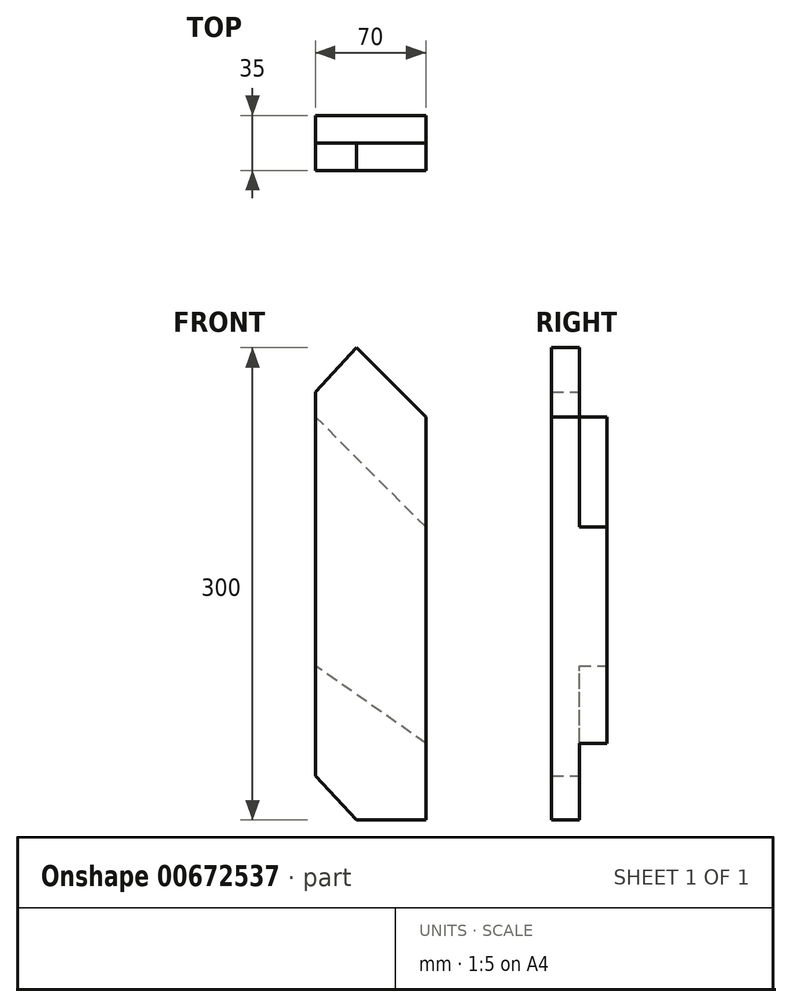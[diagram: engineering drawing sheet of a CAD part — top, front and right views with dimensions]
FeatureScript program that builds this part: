
annotation { "Feature Type Name" : "Feature", "Feature Type Description" : "" }
export const myFeature = defineFeature(function(context is Context, id is Id, definition is map)
    precondition{}
    {
        {
            var Q0;
            Q0=qCreatedBy(makeId("Front.planeOp"),FACE);
            var sketch = newSketch(context, id + "F0", { "sketchPlane" : qUnion([Q0])});
            skLineSegment(sketch, "E0.bottom", {"start": v(0, 0) * mm, "end": v(70, 0) * mm});
            skLineSegment(sketch, "E0.top", {"start": v(0, 300) * mm, "end": v(70, 300) * mm});
            skLineSegment(sketch, "E0.left", {"start": v(0, 0) * mm, "end": v(0, 300) * mm});
            skLineSegment(sketch, "E0.right", {"start": v(70, 0) * mm, "end": v(70, 300) * mm});
            skSolve(sketch);
        }
        {
            var Q0;
            Q0=makeQuery(id+"F0.imprint","IMPRINT",FACE,{"disambiguationData":[TD([[makeQuery(id+"F0.imprint","IMPRINT",EDGE,{"derivedFrom":sQuery(id+"F0.wireOp",EDGE,"E0.bottom")}),1.0]])]});
            extrude(context, id + "F1", {"entities" : qUnion([Q0]), "depth" : 35 * mm, "offsetDistance" : 25 * mm});
        }
        {
            var Q0;
            Q0=makeQuery(id+"F1.opExtrude","CAP_FACE",FACE,{"disambiguationData":[OSD([sQuery(id+"F0.wireOp",EDGE,"E0.bottom"),sQuery(id+"F0.wireOp",EDGE,"E0.top"),sQuery(id+"F0.wireOp",EDGE,"E0.left"),sQuery(id+"F0.wireOp",EDGE,"E0.right")])],"isStart":true});
            var sketch = newSketch(context, id + "F2", { "sketchPlane" : qUnion([Q0])});
            skLineSegment(sketch, "E1", {"start": v(-70, 300) * mm, "end": v(-70, 256) * mm});
            skLineSegment(sketch, "E2", {"start": v(-70, 300) * mm, "end": v(-26, 300) * mm});
            skLineSegment(sketch, "E3", {"start": v(0, 300) * mm, "end": v(0, 272) * mm});
            skLineSegment(sketch, "E4", {"start": v(-26, 300) * mm, "end": v(0, 300) * mm});
            skLineSegment(sketch, "E5", {"start": v(-26, 300) * mm, "end": v(-70, 256) * mm});
            skLineSegment(sketch, "E6", {"start": v(-26, 300) * mm, "end": v(0, 272) * mm});
            skSolve(sketch);
        }
        {
            var Q0;
            Q0=makeQuery(id+"F2.imprint","IMPRINT",FACE,{"disambiguationData":[TD([[makeQuery(id+"F2.imprint","IMPRINT",EDGE,{"derivedFrom":sQuery(id+"F2.wireOp",EDGE,"E1")}),-1.0]])]});
            var Q1;
            Q1=makeQuery(id+"F2.imprint","IMPRINT",FACE,{"disambiguationData":[TD([[makeQuery(id+"F2.imprint","IMPRINT",EDGE,{"derivedFrom":sQuery(id+"F2.wireOp",EDGE,"E3")}),1.0]])]});
            extrude(context, id + "F3", {"entities" : qUnion([Q0, Q1]), "operationType" : NewBodyOperationType.REMOVE, "endBound" : BoundingType.THROUGH_ALL, "oppositeDirection" : true, "depth" : 25 * mm, "offsetDistance" : 25 * mm});
        }
        {
            var Q0;
            Q0=makeQuery(id+"F1.opExtrude","SWEPT_FACE",FACE,{"disambiguationData":[OSD([sQuery(id+"F0.wireOp",EDGE,"E0.left")])]});
            var sketch = newSketch(context, id + "F4", { "sketchPlane" : qUnion([Q0])});
            skLineSegment(sketch, "E7", {"start": v(0, 69.18) * mm, "end": v(0, 69.18) * mm});
            skSolve(sketch);
        }
        {
            var Q0;
            Q0=makeQuery(id+"F1.opExtrude","CAP_FACE",FACE,{"disambiguationData":[OSD([sQuery(id+"F0.wireOp",EDGE,"E0.bottom"),sQuery(id+"F0.wireOp",EDGE,"E0.top"),sQuery(id+"F0.wireOp",EDGE,"E0.left"),sQuery(id+"F0.wireOp",EDGE,"E0.right")])],"isStart":true});
            var sketch = newSketch(context, id + "F5", { "sketchPlane" : qUnion([Q0])});
            skLineSegment(sketch, "E8", {"start": v(-70, 186) * mm, "end": v(0, 256) * mm});
            skSolve(sketch);
        }
        {
            var Q0;
            {var subQ3=sQuery(id+"F5.wireOp",EDGE,"E8");Q0=makeQuery(id+"F5.imprint","IMPRINT",FACE,{"disambiguationData":[TD([[makeQuery(id+"F5.imprint","IMPRINT",EDGE,{"derivedFrom":subQ3}),1.0]])]});}
            extrude(context, id + "F6", {"entities" : qUnion([Q0]), "operationType" : NewBodyOperationType.REMOVE, "oppositeDirection" : true, "depth" : 17.5 * mm, "offsetDistance" : 25 * mm});
        }
        {
            var Q0;
            Q0=makeQuery(id+"F1.opExtrude","CAP_FACE",FACE,{"disambiguationData":[OSD([sQuery(id+"F0.wireOp",EDGE,"E0.bottom"),sQuery(id+"F0.wireOp",EDGE,"E0.top"),sQuery(id+"F0.wireOp",EDGE,"E0.left"),sQuery(id+"F0.wireOp",EDGE,"E0.right")])],"isStart":true});
            var sketch = newSketch(context, id + "F7", { "sketchPlane" : qUnion([Q0])});
            skLineSegment(sketch, "E9", {"start": v(-70, 48.73) * mm, "end": v(0, 98) * mm});
            skLineSegment(sketch, "E10", {"start": v(-70, 0) * mm, "end": v(-26, 0) * mm});
            skLineSegment(sketch, "E11", {"start": v(-26, 0) * mm, "end": v(0, 0) * mm});
            skLineSegment(sketch, "E12", {"start": v(0, 0) * mm, "end": v(0, 28) * mm});
            skLineSegment(sketch, "E13", {"start": v(0, 28) * mm, "end": v(-26, 0) * mm});
            skSolve(sketch);
        }
        {
            var Q0;
            Q0=makeQuery(id+"F7.imprint","IMPRINT",FACE,{"disambiguationData":[TD([[makeQuery(id+"F7.imprint","IMPRINT",EDGE,{"derivedFrom":sQuery(id+"F7.wireOp",EDGE,"E11")}),-1.0]])]});
            extrude(context, id + "F8", {"entities" : qUnion([Q0]), "operationType" : NewBodyOperationType.REMOVE, "endBound" : BoundingType.THROUGH_ALL, "oppositeDirection" : true, "depth" : 25 * mm, "offsetDistance" : 25 * mm});
        }
        {
            var Q0;
            {var subQ0=sQuery(id+"F7.wireOp",EDGE,"E9");Q0=makeQuery(id+"F7.imprint","IMPRINT",FACE,{"disambiguationData":[TD([[makeQuery(id+"F7.imprint","IMPRINT",EDGE,{"derivedFrom":subQ0}),-1.0]])]});}
            extrude(context, id + "F9", {"entities" : qUnion([Q0]), "operationType" : NewBodyOperationType.REMOVE, "oppositeDirection" : true, "depth" : 17.5 * mm, "offsetDistance" : 25 * mm});
        }
    });
